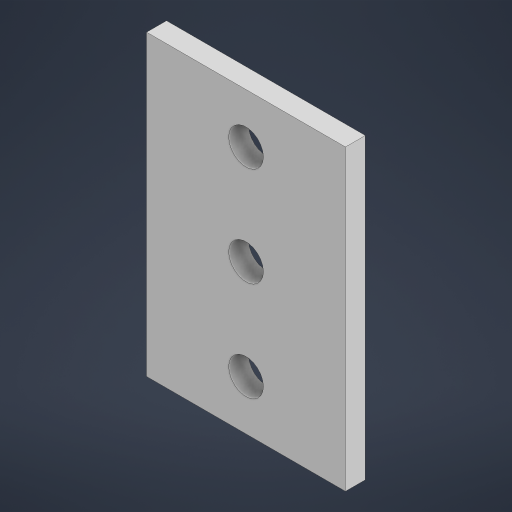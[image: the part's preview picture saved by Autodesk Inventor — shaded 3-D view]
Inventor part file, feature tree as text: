
AUTODESK INVENTOR PART (.ipt)
format: ipt  version: 2023 (Build 270158000, 158)  size: 173,056 bytes
history: native  units: mm
features: other x3, plane x1, extrude x1, sketch x1, reference x1
ambient origin geometry x8: Origin, YZ Plane, XZ Plane, XY Plane, X Axis, Y Axis, Z Axis, Center Point
bodies: Solid1 (feature_tree)
feature tree (7):
  plane  "Work Plane1"
  extrude  "Extrusion1"  [1 undecoded]
  sketch  "Sketch1"  dims[d0=2.0mm d1=0.0mm]
  reference  "Reference1"
  parser-record x1  (decoder bookkeeping rows leaked as tree rows — omitted from the tree; the rows remain in map.json)
  other  "_arm.iam"
  other  "body holder:1"
note: 1 required parameter value undecoded (feature->parameter linkage not recoverable at this tier; creation-order binding heuristic only, values carry confidence <= 0.55)
note: 1 file-system path scrubbed to <path> (originals preserved in map.json)
